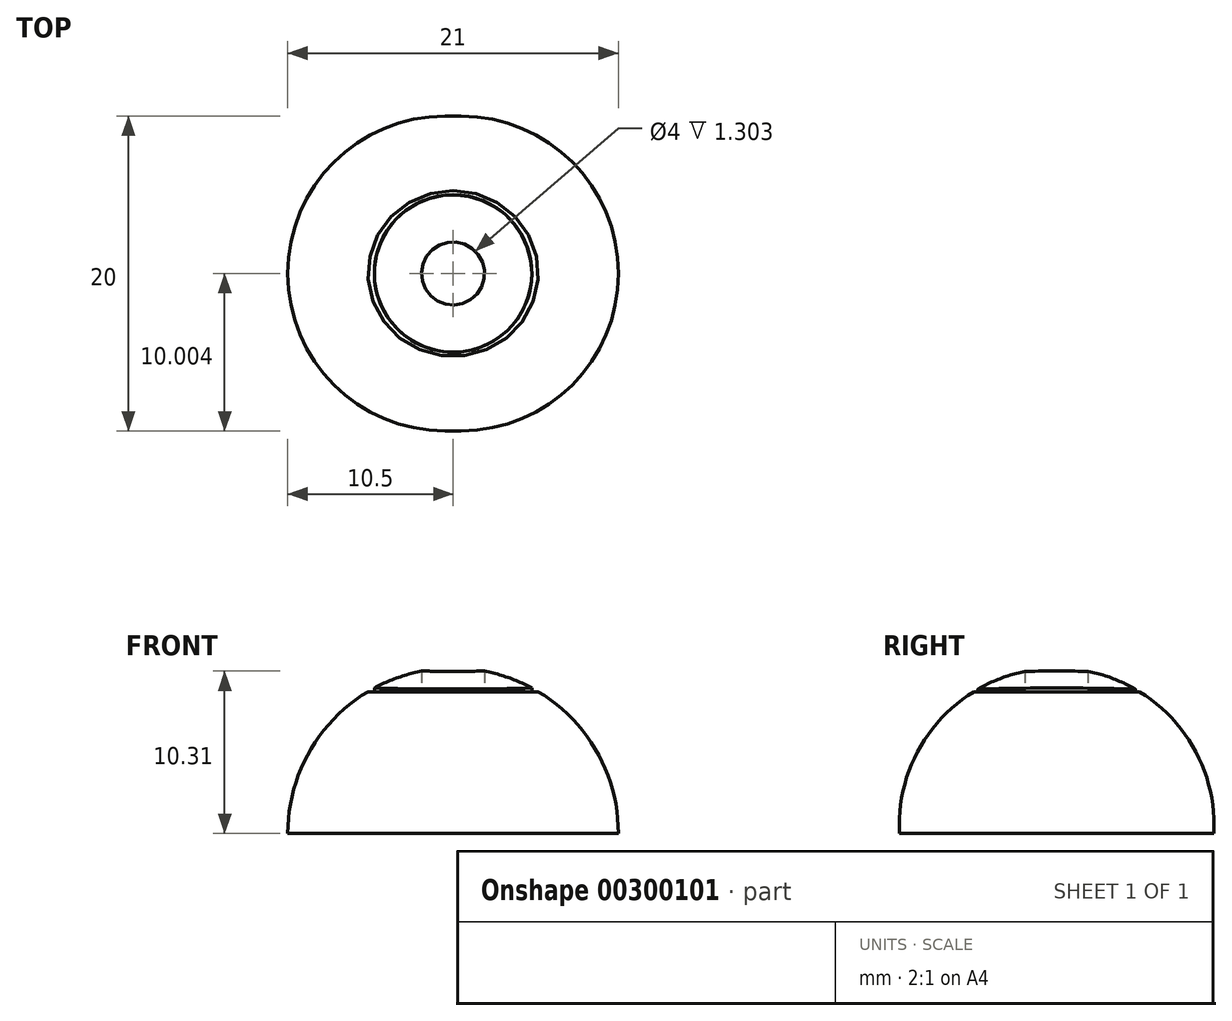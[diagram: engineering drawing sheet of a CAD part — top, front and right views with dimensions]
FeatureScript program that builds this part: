
annotation { "Feature Type Name" : "Feature", "Feature Type Description" : "" }
export const myFeature = defineFeature(function(context is Context, id is Id, definition is map)
    precondition{}
    {
        {
            var Q0;
            Q0=qCreatedBy(makeId("Top.planeOp"),FACE);
            var sketch = newSketch(context, id + "F0", { "sketchPlane" : qUnion([Q0])});
            skLineSegment(sketch, "E0", {"start": v(0, 8.59) * mm, "end": v(0, -11.21) * mm});
            skArc(sketch, "E1", {"start": v(0.5, -11.23) * mm, "mid": v(10.5, -1.23) * mm, "end": v(0.5, 8.77) * mm});
            skLineSegment(sketch, "E2", {"start": v(0, -11.21) * mm, "end": v(0, -11.23) * mm});
            skLineSegment(sketch, "E3", {"start": v(0, -11.23) * mm, "end": v(0.5, -11.23) * mm});
            skLineSegment(sketch, "E4", {"start": v(0, 8.59) * mm, "end": v(0, 8.77) * mm});
            skLineSegment(sketch, "E5", {"start": v(0, 8.77) * mm, "end": v(0.5, 8.77) * mm});
            skSolve(sketch);
        }
        {
            var Q0;
            Q0=makeQuery(id+"F0.imprint","IMPRINT",FACE,{"disambiguationData":[TD([[makeQuery(id+"F0.imprint","IMPRINT",EDGE,{"derivedFrom":sQuery(id+"F0.wireOp",EDGE,"E0")}),1.0]])]});
            var Q1;
            Q1=sQuery(id+"F0.wireOp",EDGE,"E0");
            revolve(context, id + "F1", {"entities" : qUnion([Q0]), "axis" : qUnion([Q1]), "revolveType" : RevolveType.ONE_DIRECTION, "angle" : 180 * degree});
        }
        {
            var Q0;
            Q0=qCreatedBy(makeId("Top.planeOp"),FACE);
            cPlane(context, id + "F2", {"entities" : qUnion([Q0]), "cplaneType" : CPlaneType.OFFSET, "offset" : 25 * mm, "width" : 150 * mm, "height" : 150 * mm});
        }
        {
            var Q0;
            Q0=qCreatedBy(id+"F2.planeOp",FACE);
            var sketch = newSketch(context, id + "F3", { "sketchPlane" : qUnion([Q0])});
            skCircle(sketch, "E6", {"center": v(0, -1.23) * mm, "radius": 5.5 * mm});
            skCircle(sketch, "E7", {"center": v(0, -1.23) * mm, "radius": 5 * mm});
            skSolve(sketch);
        }
        {
            var Q0;
            Q0 = qSketchRegion(id + "F3", true);
            extrude(context, id + "F4", {"entities" : qUnion([Q0]), "operationType" : NewBodyOperationType.REMOVE, "oppositeDirection" : true, "depth" : 16 * mm});
        }
        {
            var Q0;
            Q0=makeQuery(id+"F4.boolean.opBoolean","COPY",FACE,{"derivedFrom":makeQuery(id+"F4.opExtrude","CAP_FACE",FACE,{"disambiguationData":[OSD([sQuery(id+"F3.wireOp",EDGE,"E6")])],"isStart":false})});
            var sketch = newSketch(context, id + "F5", { "sketchPlane" : qUnion([Q0])});
            skCircle(sketch, "E8", {"center": v(0, -1.23) * mm, "radius": 2 * mm});
            skSolve(sketch);
        }
        {
            var Q0;
            Q0 = qSketchRegion(id + "F5", true);
            extrude(context, id + "F6", {"entities" : qUnion([Q0]), "operationType" : NewBodyOperationType.REMOVE, "depth" : 5 * mm});
        }
    });
